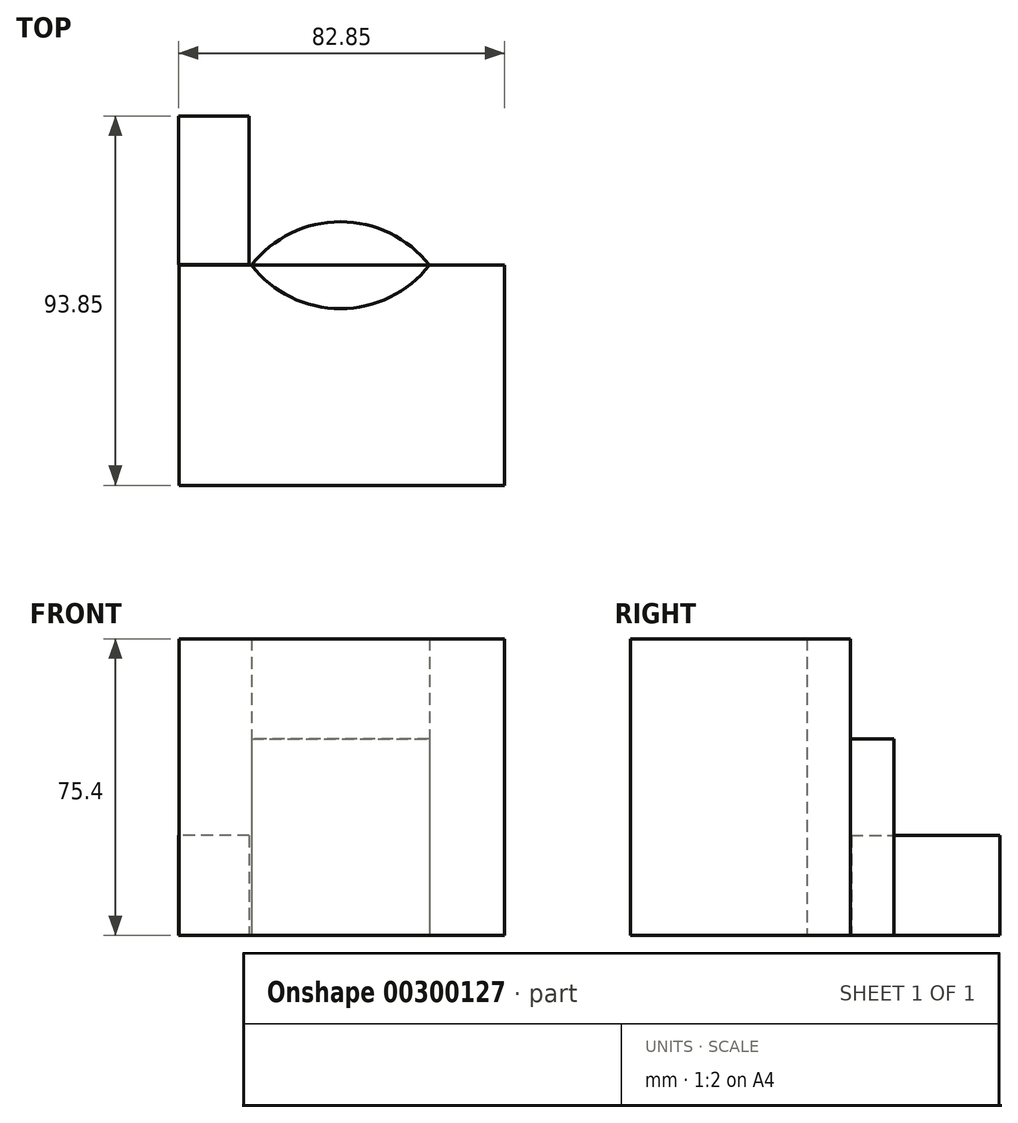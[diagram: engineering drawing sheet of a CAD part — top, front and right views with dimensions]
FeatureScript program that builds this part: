
annotation { "Feature Type Name" : "Feature", "Feature Type Description" : "" }
export const myFeature = defineFeature(function(context is Context, id is Id, definition is map)
    precondition{}
    {
        {
            var Q0;
            Q0=qCreatedBy(makeId("Top.planeOp"),FACE);
            var sketch = newSketch(context, id + "F0", { "sketchPlane" : qUnion([Q0])});
            skLineSegment(sketch, "E0.bottom", {"start": v(-41.71, 35.45) * mm, "end": v(40.95, 35.45) * mm});
            skLineSegment(sketch, "E0.top", {"start": v(-41.71, -20.48) * mm, "end": v(40.95, -20.48) * mm});
            skLineSegment(sketch, "E0.left", {"start": v(-41.71, 35.45) * mm, "end": v(-41.71, -20.48) * mm});
            skLineSegment(sketch, "E0.right", {"start": v(40.95, 35.45) * mm, "end": v(40.95, -20.48) * mm});
            skArc(sketch, "E1", {"start": v(21.86, 35.45) * mm, "mid": v(-0.73, 46.5) * mm, "end": v(-23.32, 35.45) * mm});
            skArc(sketch, "E2.MirrorCS", {"start": v(21.86, 35.45) * mm, "mid": v(-0.73, 24.41) * mm, "end": v(-23.32, 35.45) * mm});
            skSolve(sketch);
        }
        {
            var Q0;
            Q0=makeQuery(id+"F0.imprint","IMPRINT",FACE,{"disambiguationData":[TD([[makeQuery(id+"F0.imprint","IMPRINT",EDGE,{"derivedFrom":sQuery(id+"F0.wireOp",EDGE,"E0.top")}),1.0]])]});
            var Q1;
            {var subQ1=sQuery(id+"F0.wireOp",EDGE,"E1");Q1=makeQuery(id+"F0.imprint","IMPRINT",FACE,{"disambiguationData":[TD([[makeQuery(id+"F0.imprint","IMPRINT",EDGE,{"derivedFrom":subQ1}),1.0]])]});}
            extrude(context, id + "F1", {"entities" : qUnion([Q0, Q1]), "depth" : 50 * mm});
        }
        {
            var Q0;
            Q0=qCreatedBy(makeId("Top.planeOp"),FACE);
            var sketch = newSketch(context, id + "F2", { "sketchPlane" : qUnion([Q0])});
            skLineSegment(sketch, "E3.bottom", {"start": v(-23.89, 35.64) * mm, "end": v(-41.9, 35.64) * mm});
            skLineSegment(sketch, "E3.top", {"start": v(-23.89, 73.37) * mm, "end": v(-41.9, 73.37) * mm});
            skLineSegment(sketch, "E3.left", {"start": v(-23.89, 35.64) * mm, "end": v(-23.89, 73.37) * mm});
            skLineSegment(sketch, "E3.right", {"start": v(-41.9, 35.64) * mm, "end": v(-41.9, 73.37) * mm});
            skSolve(sketch);
        }
        {
            var Q0;
            Q0=makeQuery(id+"F1.opExtrude","CAP_FACE",FACE,{"disambiguationData":[OSD([sQuery(id+"F0.wireOp",EDGE,"E0.bottom"),sQuery(id+"F0.wireOp",EDGE,"E0.top"),sQuery(id+"F0.wireOp",EDGE,"E0.left"),sQuery(id+"F0.wireOp",EDGE,"E0.right"),sQuery(id+"F0.wireOp",EDGE,"E2.MirrorCS")])],"isStart":false});
            var Q1;
            Q1=makeQuery(id+"F2.imprint","IMPRINT",FACE,{"disambiguationData":[TD([[makeQuery(id+"F2.imprint","IMPRINT",EDGE,{"derivedFrom":sQuery(id+"F2.wireOp",EDGE,"E3.bottom")}),-1.0]])]});
            extrude(context, id + "F3", {"entities" : qUnion([Q0, Q1]), "operationType" : NewBodyOperationType.ADD, "depth" : 25.4 * mm});
        }
    });
